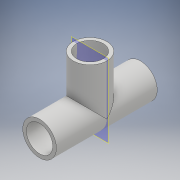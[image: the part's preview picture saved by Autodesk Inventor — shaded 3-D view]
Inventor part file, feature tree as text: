
AUTODESK INVENTOR PART (.ipt)
format: ipt  version: 2017 (Build 210142000, 142)  size: 117,248 bytes
history: native  units: mm
features: extrude x2, sketch x2, plane x1, shell x1
ambient origin geometry x8: Origin, YZ Plane, XZ Plane, XY Plane, X Axis, Y Axis, Z Axis, Center Point
bodies: Solid1 (feature_tree)
feature tree (6):
  extrude  "Extrusion1"  Depth=84.0mm TaperAngle=0.0deg
  plane  "Work Plane1"
  extrude  "Extrusion2"  Depth=42.0mm
  shell  "Shell1"  Thickness=100.0mm
  sketch  "Sketch1"  dims[d0=28.0mm d1=84.0mm d2=0.0mm]
  sketch  "Sketch2"  dims[d3=42.0mm d4=28.0mm d5=100.0mm d6=0.0mm d7=3.0mm]
